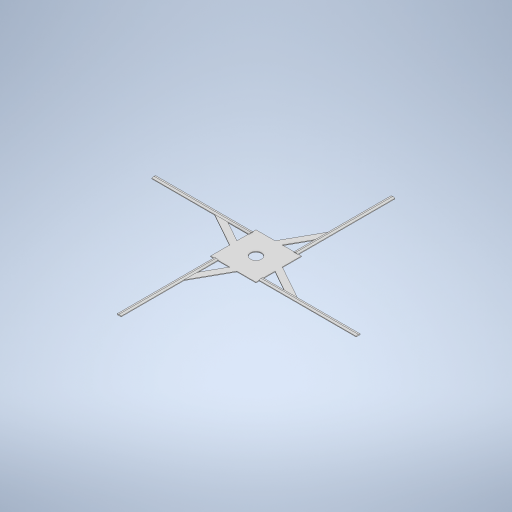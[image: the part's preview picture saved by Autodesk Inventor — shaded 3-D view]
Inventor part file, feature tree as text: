
AUTODESK INVENTOR PART (.ipt)
format: ipt  version: 2024 (Build 280153000, 153)  size: 400,384 bytes
history: native  units: in
note: dims shown in document units (in); Inventor stores cm internally (conversion verified against a paired STEP export)
features: extrude x5, sketch x5
ambient origin geometry x8: Origin, YZ Plane, XZ Plane, XY Plane, X Axis, Y Axis, Z Axis, Center Point
bodies: Solid1 (feature_tree)
feature tree (10):
  extrude  "Extrusion1"  Depth=0.473in
  sketch  "Sketch3"  dims[d2=0.02in d3=0.0in d8=0.473in]
  extrude  "Extrusion4"  Depth=0.473in
  extrude  "Extrusion5"  Depth=1.5in
  extrude  "Extrusion6"  Depth=0.063in
  extrude  "Extrusion7"  TaperAngle=45.0deg  [1 undecoded]
  sketch  "Sketch1"  dims[d0=3.688in d1=0.473in]
  sketch  "Sketch6"  dims[d9=0.063in d10=1.5in]
  sketch  "Sketch7"  dims[d11=1.5748in d13=360.0deg d15=0.063in]
  sketch  "Sketch9"  dims[d16=0.5in d17=45.0deg d19=0.277in d20=1.5748in d22=360.0deg d24=0.268in d25=0.268in d26=0.17in d27=1.5748in d29=360.0deg d31=0.05in d32=1.5748in d34=360.0deg d37=0.4in d40=0.2in d41=0.2in d42=0.2in d43=0.2in d44=0.7874in d46=180.0deg d53=0.17in d55=0.2477in d56=0.1in d57=0.0in d58=0.0in d59=0.0in d60=0.0in d61=0.0in d62=0.7in d63=0.17in d65=0.2in d66=0.6in d67=1.5748in d69=360.0deg d71=0.01in d72=0.0in]
note: 1 required parameter value undecoded (feature->parameter linkage not recoverable at this tier; creation-order binding heuristic only, values carry confidence <= 0.55)
